# Revit family: VLN_Nim-II-Mes-E_Multiproduct_BIM_NL_F3082;F3083
name_source: partatom
category: Plumbing Fixtures
revit_build: Autodesk Revit MEP 2014 (Build: 20130308_1515(x64)
units: mm (PartAtom-declared; Revit-internal decimal feet)

## types (2) — shared parameters
AreaUnits = millimeters
Assembly Code = C1030200
BREEAMApproved = No
Brand = Ideal Standard
Default Elevation = 800 mm  [stored 2.62467 ft]
ECA = No
IfcExportAs = IfcValveType
IfcExportType = FAUCET
LinearUnits = millimeters
NBSDescription = Shower mixers
NBSReference = 45-35-70/335
NominalHeight = 62 mm
NominalLength = 88 mm
NominalWidth = 39 mm
Size = 40 x 88 x 62 mm
TMV3 = Yes
TestPressure = 10 Bar
URL = www.idealstandardnederland.nl
Uniclass2015Code = Pr_40_20_87_78
Uniclass2015Title = Shower manual water supply sets
Uniclass2015Version = Products v1.1
Version = 1
VolumeUnits = liter
WRAS = No
WarrantyDescription = Fabrieksgarantie
WarrantyDurationUnit = jaar
WaterEfficientProduct = No
zero-valued in all types: CWFU, Cost, HWFU, WFU

## per-type parameters (varying)
| type | BIMObjectName | F3083AA | Model | ModelNumber | Name |
| F3082AA - NIM WASM/VAATW KR BELUCHT 1/2 X 3/4 | ISI_IdealStandard_ShowerManualWaterSupplySets_F3082AA | No | F3082AA | F3082AA | ShowerManualWaterSupplySets_F3082AA_IdealStandard |
| F3083AA - NIM WASM/VAATW KR KEERKL BEL 1/2 X 3/4 | ISI_IdealStandard_ShowerManualWaterSupplySets_F3083AA | Yes | F3083AA | F3083AA | ShowerManualWaterSupplySets_F3083AA_IdealStandard |

note: [stored X ft] marks values corroborated as IEEE doubles in the binary element streams (Revit-internal decimal feet)

## geometry (parser evidence)
native form markers: Sweep x1
no freeform markers — native parametric forms only
